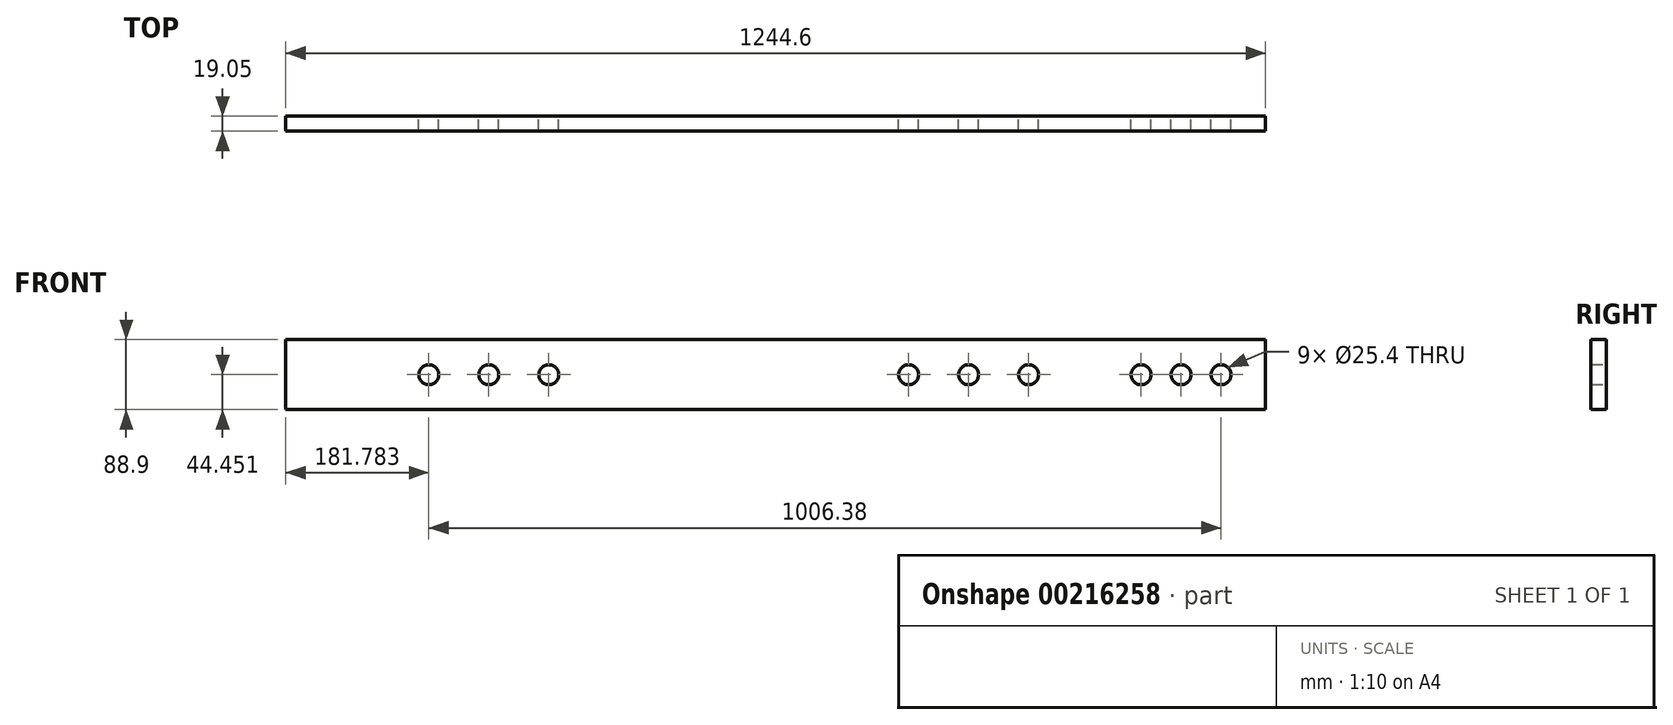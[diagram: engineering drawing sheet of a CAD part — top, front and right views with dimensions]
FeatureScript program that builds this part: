
annotation { "Feature Type Name" : "Feature", "Feature Type Description" : "" }
export const myFeature = defineFeature(function(context is Context, id is Id, definition is map)
    precondition{}
    {
        {
            var Q0;
            Q0=qCreatedBy(makeId("Front.planeOp"),FACE);
            var sketch = newSketch(context, id + "F0", { "sketchPlane" : qUnion([Q0])});
            skLineSegment(sketch, "E0", {"start": v(-2709.55, -2746.5) * mm, "end": v(-1464.95, -2746.5) * mm});
            skLineSegment(sketch, "E1", {"start": v(-1464.95, -2743.33) * mm, "end": v(-1464.95, -2838.58) * mm});
            skLineSegment(sketch, "E2", {"start": v(-1464.95, -2835.4) * mm, "end": v(-2709.55, -2835.4) * mm});
            skLineSegment(sketch, "E3", {"start": v(-2709.55, -2838.58) * mm, "end": v(-2709.55, -2743.33) * mm});
            skCircle(sketch, "E4", {"center": v(-1521.39, -2790.96) * mm, "radius": 12.7 * mm});
            skCircle(sketch, "E5", {"center": v(-1572.19, -2790.96) * mm, "radius": 12.7 * mm});
            skCircle(sketch, "E6", {"center": v(-1622.99, -2790.96) * mm, "radius": 12.7 * mm});
            skCircle(sketch, "E7", {"center": v(-2375.37, -2790.96) * mm, "radius": 12.7 * mm});
            skCircle(sketch, "E8", {"center": v(-2451.57, -2790.96) * mm, "radius": 12.7 * mm});
            skCircle(sketch, "E9", {"center": v(-2527.77, -2790.96) * mm, "radius": 12.7 * mm});
            skCircle(sketch, "E10", {"center": v(-1765.86, -2790.96) * mm, "radius": 12.7 * mm});
            skCircle(sketch, "E11", {"center": v(-1842.06, -2790.96) * mm, "radius": 12.7 * mm});
            skCircle(sketch, "E12", {"center": v(-1918.26, -2790.96) * mm, "radius": 12.7 * mm});
            skLineSegment(sketch, "E13", {"start": v(-2709.55, -2790.96) * mm, "end": v(-1464.95, -2790.96) * mm, "construction": true});
            skSolve(sketch);
        }
        {
            var Q0;
            Q0=makeQuery(id+"F0.imprint","IMPRINT",FACE,{"disambiguationData":[TD([[makeQuery(id+"F0.imprint","IMPRINT",EDGE,{"derivedFrom":sQuery(id+"F0.wireOp",EDGE,"E0")}),-1.0]])]});
            extrude(context, id + "F1", {"entities" : qUnion([Q0]), "depth" : 19.05 * mm});
        }
    });
